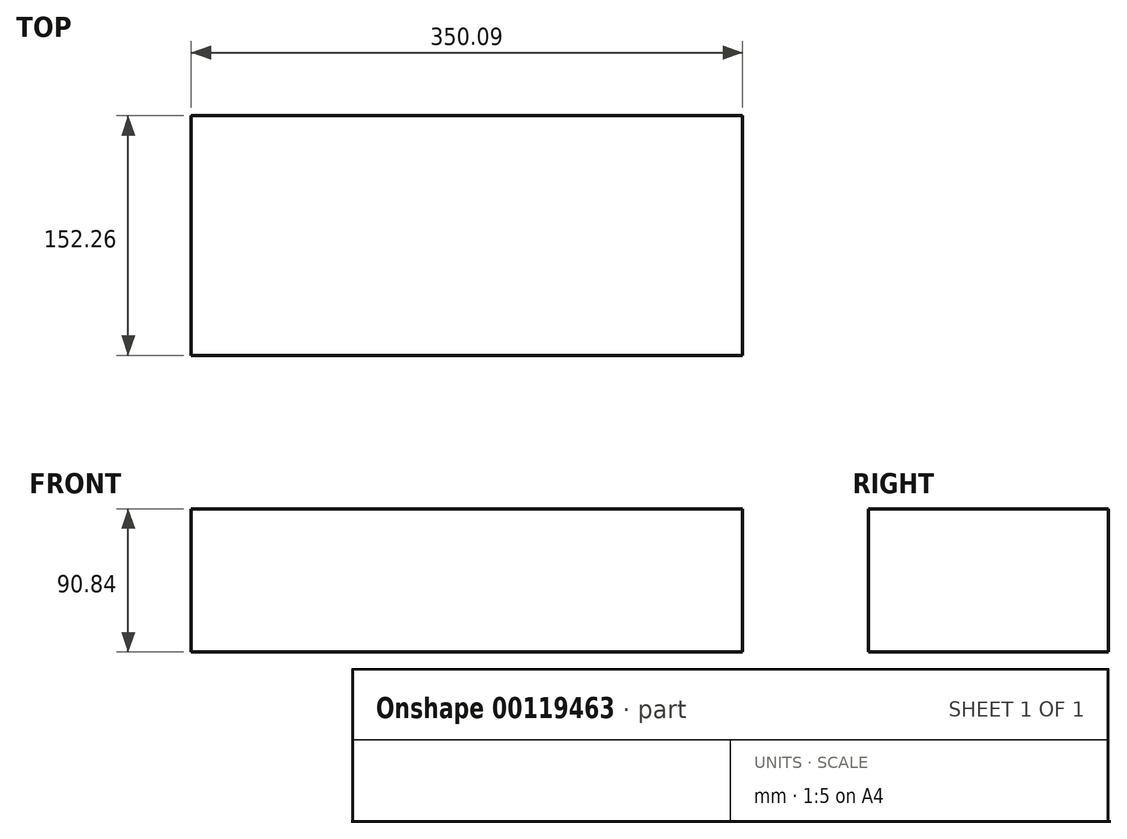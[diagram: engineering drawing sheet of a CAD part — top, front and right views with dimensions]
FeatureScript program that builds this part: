
annotation { "Feature Type Name" : "Feature", "Feature Type Description" : "" }
export const myFeature = defineFeature(function(context is Context, id is Id, definition is map)
    precondition{}
    {
        {
            var Q0;
            Q0=qCreatedBy(makeId("Right.planeOp"),FACE);
            var sketch = newSketch(context, id + "F0", { "sketchPlane" : qUnion([Q0])});
            skLineSegment(sketch, "E0.bottom", {"start": v(-76.13, 45.42) * mm, "end": v(76.13, 45.42) * mm});
            skLineSegment(sketch, "E0.top", {"start": v(-76.13, -45.42) * mm, "end": v(76.13, -45.42) * mm});
            skLineSegment(sketch, "E0.left", {"start": v(-76.13, 45.42) * mm, "end": v(-76.13, -45.42) * mm});
            skLineSegment(sketch, "E0.right", {"start": v(76.13, 45.42) * mm, "end": v(76.13, -45.42) * mm});
            skPoint(sketch, "E0.middle", {"position": v(0, 0) * mm});
            skSolve(sketch);
        }
        {
            var Q0;
            Q0 = qSketchRegion(id + "F0", true);
            extrude(context, id + "F1", {"entities" : qUnion([Q0]), "depth" : 350.1 * mm});
        }
    });
